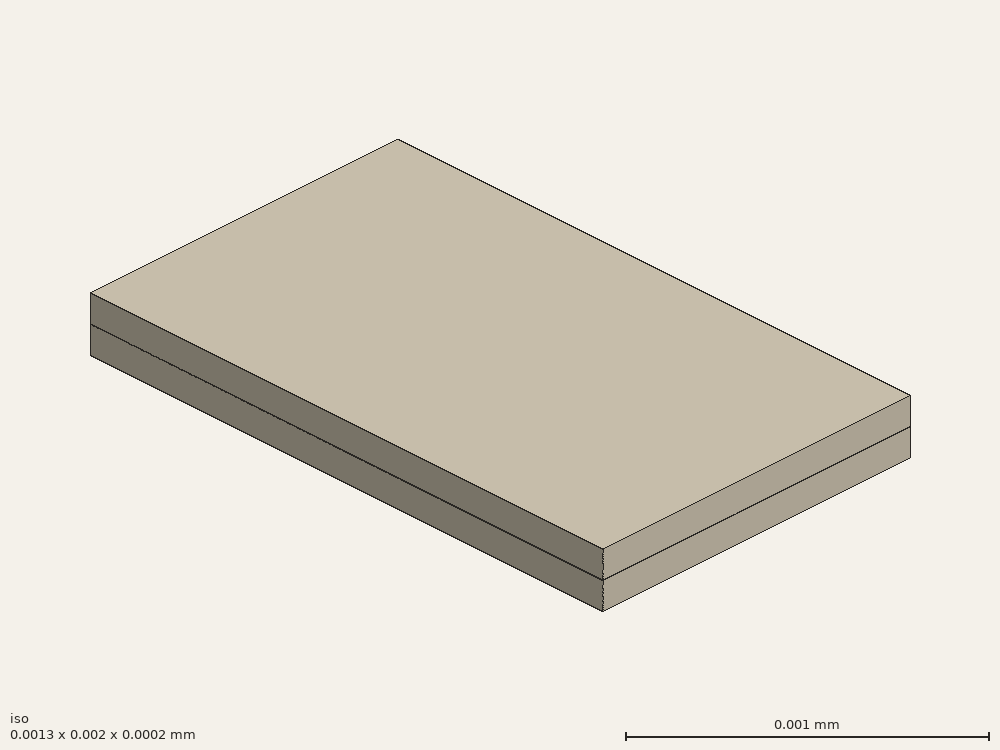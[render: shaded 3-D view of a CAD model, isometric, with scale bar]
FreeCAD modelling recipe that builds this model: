
FCSTD DOCUMENT  (FreeCAD 0.21R33694 (Git))
Label: diffPair
License: All rights reserved
LicenseURL: http://en.wikipedia.org/wiki/All_rights_reserved
objects: Part::Part2DObjectPython×23, App::FeaturePython×12, Part::Extrusion×5, Part::Cut×3, Part::FeaturePython×2
note: 33 computed .brp shape members not serialized (recipe doc carries the construction recipe); baked Part::Feature solids carry a one-line shape summary decoded from their .brp

FEATURE [Part::Part2DObjectPython] Wire  # Draft 2D object (typed FeaturePython)
  Area = 0.0014181
  ChamferSize = 0
  Closed = true
  End = (-0.05,0,0)
  FilletRadius = 0
  Length = 0.221006
  MakeFace = true
  Placement = pos=(-0.15,0,0) rot=(0,0,1;0rad)
  Points = (4) [(0,0,0),(0.00545955,0.015,0),(0.0945402,0.015,0),(0.1,-6.12323e-18,0)]
  Start = (-0.15,0,0)
  Subdivisions = 0
FEATURE [Part::Part2DObjectPython] Wire001  # Draft 2D object (typed FeaturePython)
  Area = 0.0014181
  ChamferSize = 0
  Closed = true
  End = (0.15,0,0)
  FilletRadius = 0
  Length = 0.221006
  MakeFace = true
  Placement = pos=(0.05,0,0) rot=(0,0,1;0rad)
  Points = (4) [(0,0,0),(0.00545955,0.015,0),(0.0945402,0.015,0),(0.1,-6.12323e-18,0)]
  Start = (0.05,0,0)
  Subdivisions = 0
FEATURE [Part::Part2DObjectPython] Rectangle  # Draft 2D object (typed FeaturePython)
  Area = 0.13
  ChamferSize = 0
  Columns = 1
  FilletRadius = 0
  Height = 0.1
  Length = 1.3
  MakeFace = true
  Placement = pos=(-0.65,-0.1,0) rot=(0,0,1;0rad)
  Rows = 1
FEATURE [Part::Part2DObjectPython] Rectangle001  # Draft 2D object (typed FeaturePython)
  Area = 0.13
  ChamferSize = 0
  Columns = 1
  FilletRadius = 0
  Height = 0.1
  Length = 1.3
  MakeFace = true
  Placement = pos=(-0.65,0,0) rot=(0,0,1;0rad)
  Rows = 1
FEATURE [Part::Part2DObjectPython] Clone2D  label="Wire (2D)"  # Draft 2D object (typed FeaturePython)
  Fuse = false
  Objects = -> [Wire]
  Placement = pos=(-0.15,0,0) rot=(0,0,1;0rad)
  Scale = (1,1,1)
FEATURE [Part::Part2DObjectPython] Clone2D001  label="Wire001 (2D)"  # Draft 2D object (typed FeaturePython)
  Fuse = false
  Objects = -> [Wire001]
  Placement = pos=(0.05,0,0) rot=(0,0,1;0rad)
  Scale = (1,1,1)
FEATURE [Part::Part2DObjectPython] Clone2D002  label="Rectangle (2D)"  # Draft 2D object (typed FeaturePython)
  Fuse = false
  Objects = -> [Rectangle]
  Placement = pos=(-0.65,-0.1,0) rot=(0,0,1;0rad)
  Scale = (1,1,1)
FEATURE [Part::Part2DObjectPython] Clone2D003  label="Rectangle001 (2D)"  # Draft 2D object (typed FeaturePython)
  Fuse = false
  Objects = -> [Rectangle001]
  Placement = pos=(-0.65,0,0) rot=(0,0,1;0rad)
  Scale = (1,1,1)
FEATURE [Part::Part2DObjectPython] Clone2D004  label="Wire (2D)001"  # Draft 2D object (typed FeaturePython)
  Fuse = false
  Objects = -> [Wire]
  Placement = pos=(-0.15,0,0) rot=(0,0,1;0rad)
  Scale = (1,1,1)
FEATURE [Part::Part2DObjectPython] Clone2D005  label="Wire001 (2D)001"  # Draft 2D object (typed FeaturePython)
  Fuse = false
  Objects = -> [Wire001]
  Placement = pos=(0.05,0,0) rot=(0,0,1;0rad)
  Scale = (1,1,1)
FEATURE [Part::Part2DObjectPython] Clone2D006  label="Rectangle (2D)001"  # Draft 2D object (typed FeaturePython)
  Fuse = false
  Objects = -> [Rectangle]
  Placement = pos=(-0.65,-0.1,0) rot=(0,0,1;0rad)
  Scale = (1,1,1)
FEATURE [Part::Part2DObjectPython] Clone2D007  label="Rectangle001 (2D)001"  # Draft 2D object (typed FeaturePython)
  Fuse = false
  Objects = -> [Rectangle001]
  Placement = pos=(-0.65,0,0) rot=(0,0,1;0rad)
  Scale = (1,1,1)
FEATURE [Part::Extrusion] Extrude004
  Base = -> Clone2D
  Dir = (0,0,1)
  DirMode = 2
  FaceMakerClass = Part::FaceMakerBullseye
  LengthFwd = 2
  LengthRev = 0
  Solid = false
  Symmetric = false
FEATURE [Part::Extrusion] Extrude005
  Base = -> Clone2D001
  Dir = (0,0,1)
  DirMode = 2
  FaceMakerClass = Part::FaceMakerBullseye
  LengthFwd = 2
  LengthRev = 0
  Solid = false
  Symmetric = false
FEATURE [Part::Extrusion] Extrude006
  Base = -> Clone2D002
  Dir = (0,0,1)
  DirMode = 2
  FaceMakerClass = Part::FaceMakerBullseye
  LengthFwd = 2
  LengthRev = 0
  Solid = false
  Symmetric = false
FEATURE [Part::Extrusion] Extrude007
  Base = -> Clone2D003
  Dir = (0,0,1)
  DirMode = 2
  FaceMakerClass = Part::FaceMakerBullseye
  LengthFwd = 2
  LengthRev = 0
  Solid = false
  Symmetric = false
FEATURE [Part::Cut] Cut002
  Base = -> Extrude007
  Tool = -> Extrude004
FEATURE [Part::Cut] Cut003
  Base = -> Cut002
  Tool = -> Extrude005
FEATURE [App::FeaturePython] Text010  label="_Sin(PV){port1}"  # WARN: FeaturePython — macro-defined, semantics opaque (R4)
  Placement = pos=(5.00075,-5.09743,10) rot=(0,0,1;0rad)
  Text = .
FEATURE [App::FeaturePython] Text011  label="_Sout(PV){port2}"  # WARN: FeaturePython — macro-defined, semantics opaque (R4)
  Placement = pos=(5.00075,-5.09743,10) rot=(0,0,1;0rad)
  Text = .
FEATURE [App::FeaturePython] Text012  label="_Lin(1,voltage,in1){v11}"  # WARN: FeaturePython — macro-defined, semantics opaque (R4)
  Placement = pos=(5.00075,-5.09743,10) rot=(0,0,1;0rad)
  Text = .
FEATURE [App::FeaturePython] Text013  label="_Lin(1,current,in1){i11}"  # WARN: FeaturePython — macro-defined, semantics opaque (R4)
  Placement = pos=(5.00075,-5.09743,10) rot=(0,0,1;0rad)
  Text = .
FEATURE [App::FeaturePython] Text014  label="_Lin(2,voltage,in2){v12}"  # WARN: FeaturePython — macro-defined, semantics opaque (R4)
  Placement = pos=(5.00075,-5.09743,10) rot=(0,0,1;0rad)
  Text = .
FEATURE [App::FeaturePython] Text015  label="_Lin(2,current,in2){i12}"  # WARN: FeaturePython — macro-defined, semantics opaque (R4)
  Placement = pos=(5.00075,-5.09743,10) rot=(0,0,1;0rad)
  Text = .
FEATURE [App::FeaturePython] Text016  label="_Lout(3,voltage,out3){v21}"  # WARN: FeaturePython — macro-defined, semantics opaque (R4)
  Placement = pos=(5.00075,-5.09743,10) rot=(0,0,1;0rad)
  Text = .
FEATURE [App::FeaturePython] Text017  label="_Lout(3,current,out3){i21}"  # WARN: FeaturePython — macro-defined, semantics opaque (R4)
  Placement = pos=(5.00075,-5.09743,10) rot=(0,0,1;0rad)
  Text = .
FEATURE [App::FeaturePython] Text018  label="_Lout(4,voltage,out4){v22}"  # WARN: FeaturePython — macro-defined, semantics opaque (R4)
  Placement = pos=(5.00075,-5.09743,10) rot=(0,0,1;0rad)
  Text = .
FEATURE [App::FeaturePython] Text019  label="_Lout(4,current,out4){i22}"  # WARN: FeaturePython — macro-defined, semantics opaque (R4)
  Placement = pos=(5.00075,-5.09743,10) rot=(0,0,1;0rad)
  Text = .
FEATURE [Part::Part2DObjectPython] Wire006  label="_Pi22"  # Draft 2D object (typed FeaturePython)
  Area = 1.4181e-09
  ChamferSize = 0
  Closed = true
  End = (5e-05,-0.0999,4.995)
  FilletRadius = 0
  Length = 0.000221006
  MakeFace = true
  Placement = pos=(0.00015,-0.0999,4.995) rot=(0.57735,0.57735,0.57735;4.18879rad)
  Points = (4) [(0,0,0),(1.5e-05,-5.45983e-06,0),(1.5e-05,-9.45404e-05,0),(0,-0.0001,0)]
  Start = (0.00015,-0.0999,4.995)
  Subdivisions = 0
FEATURE [Part::Part2DObjectPython] Wire007  label="_Pi21"  # Draft 2D object (typed FeaturePython)
  Area = 1.4181e-09
  ChamferSize = 0
  Closed = true
  End = (-0.00015,-0.0999,4.995)
  FilletRadius = 0
  Length = 0.000221006
  MakeFace = true
  Placement = pos=(-5e-05,-0.0999,4.995) rot=(0.57735,0.57735,0.57735;4.18879rad)
  Points = (4) [(0,0,0),(1.5e-05,-5.45983e-06,0),(1.5e-05,-9.45404e-05,0),(0,-0.0001,0)]
  Start = (-5e-05,-0.0999,4.995)
  Subdivisions = 0
FEATURE [Part::Part2DObjectPython] Wire008  label="_Pi11"  # Draft 2D object (typed FeaturePython)
  Area = 1.4181e-09
  ChamferSize = 0
  Closed = true
  End = (-5e-05,-0.1019,4.995)
  FilletRadius = 0
  Length = 0.000221006
  MakeFace = true
  Placement = pos=(-0.00015,-0.1019,4.995) rot=(1,0,0;1.5708rad)
  Points = (4) [(0,0,0),(5.45955e-06,1.5e-05,0),(9.45402e-05,1.5e-05,0),(0.0001,0,0)]
  Start = (-0.00015,-0.1019,4.995)
  Subdivisions = 0
FEATURE [Part::Part2DObjectPython] Wire009  label="_Pi12"  # Draft 2D object (typed FeaturePython)
  Area = 1.4181e-09
  ChamferSize = 0
  Closed = true
  End = (0.00015,-0.1019,4.995)
  FilletRadius = 0
  Length = 0.000221006
  MakeFace = true
  Placement = pos=(5e-05,-0.1019,4.995) rot=(1,0,0;1.5708rad)
  Points = (4) [(0,0,0),(5.45955e-06,1.5e-05,0),(9.45402e-05,1.5e-05,0),(0.0001,0,0)]
  Start = (5e-05,-0.1019,4.995)
  Subdivisions = 0
FEATURE [Part::Part2DObjectPython] Rectangle013  label="_Pport1"  # Draft 2D object (typed FeaturePython)
  Area = 2.6e-07
  ChamferSize = 0
  Columns = 1
  FilletRadius = 0
  Height = 0.0002
  Length = 0.0013
  MakeFace = true
  Placement = pos=(-0.00065,-0.1019,4.9949) rot=(1,0,0;1.5708rad)
  Rows = 1
FEATURE [Part::Part2DObjectPython] Line  label="_Pv11"  # Draft 2D object (typed FeaturePython)
  Area = 0
  ChamferSize = 0
  Closed = false
  End = (-0.0001,-0.1019,4.995)
  FilletRadius = 0
  Length = 0.0001
  MakeFace = true
  Placement = pos=(0,-0.1019,4.9949) rot=(1,0,0;1.5708rad)
  Points = (2) [(-0.0001,0,0),(-0.0001,0.0001,0)]
  Start = (-0.0001,-0.1019,4.9949)
  Subdivisions = 0
FEATURE [Part::Part2DObjectPython] Line004  label="_Pv12"  # Draft 2D object (typed FeaturePython)
  Area = 0
  ChamferSize = 0
  Closed = false
  End = (0.0001,-0.1019,4.995)
  FilletRadius = 0
  Length = 0.0001
  MakeFace = true
  Placement = pos=(0,-0.1019,4.9949) rot=(1,0,0;1.5708rad)
  Points = (2) [(0.0001,0,0),(0.0001,0.0001,0)]
  Start = (0.0001,-0.1019,4.9949)
  Subdivisions = 0
FEATURE [Part::Part2DObjectPython] Rectangle014  label="_Pport2"  # Draft 2D object (typed FeaturePython)
  Area = 2.6e-07
  ChamferSize = 0
  Columns = 1
  FilletRadius = 0
  Height = 0.0013
  Length = 0.0002
  MakeFace = true
  Placement = pos=(-0.00065,-0.0999,4.9949) rot=(0.57735,0.57735,0.57735;4.18879rad)
  Rows = 1
FEATURE [Part::Part2DObjectPython] Line005  label="_Pv21"  # Draft 2D object (typed FeaturePython)
  Area = 0
  ChamferSize = 0
  Closed = false
  End = (-0.0001,-0.0999,4.995)
  FilletRadius = 0
  Length = 0.0001
  MakeFace = true
  Placement = pos=(0,-0.0999,4.9949) rot=(0.57735,0.57735,0.57735;4.18879rad)
  Points = (2) [(1.38778e-17,-0.0001,0),(0.0001,-0.0001,0)]
  Start = (-0.0001,-0.0999,4.9949)
  Subdivisions = 0
FEATURE [Part::Part2DObjectPython] Line006  label="_Pv22"  # Draft 2D object (typed FeaturePython)
  Area = 0
  ChamferSize = 0
  Closed = false
  End = (0.0001,-0.0999,4.995)
  FilletRadius = 0
  Length = 0.0001
  MakeFace = true
  Placement = pos=(0,-0.0999,4.9949) rot=(0.57735,0.57735,0.57735;4.18879rad)
  Points = (2) [(1.38778e-17,0.0001,0),(0.0001,0.0001,0)]
  Start = (0.0001,-0.0999,4.9949)
  Subdivisions = 0
FEATURE [Part::Part2DObjectPython] Rectangle015  # Draft 2D object (typed FeaturePython)
  Area = 0.01
  ChamferSize = 0
  Columns = 1
  FilletRadius = 0
  Height = 0.1
  Length = 0.1
  MakeFace = true
  Placement = pos=(-0.15,0,2.45) rot=(1,0,0;1.5708rad)
  Rows = 1
FEATURE [Part::Extrusion] Extrude
  Base = -> Rectangle015
  Dir = (0,-1,2e-16)
  DirMode = 2
  FaceMakerClass = Part::FaceMakerBullseye
  LengthFwd = 0.1
  LengthRev = 0
  Placement = pos=(0,0,-1.5) rot=(0,0,1;0rad)
  Solid = false
  Symmetric = false
FEATURE [Part::Cut] Cut
  Base = -> Extrude006
  Tool = -> Extrude
FEATURE [Part::FeaturePython] BooleanFragments  # WARN: FeaturePython — macro-defined, semantics opaque (R4)
  Mode = 0
  Objects = -> [Cut003,Cut]
  Tolerance = 0
FEATURE [Part::FeaturePython] Clone  label="scaled"  # Draft clone (typed FeaturePython)
  AttacherType = Attacher::AttachEngine3D
  Fuse = false
  Objects = -> [BooleanFragments]
  Placement = pos=(0,-0.0999,4.995) rot=(1,0,0;1.5708rad)
  Scale = (0.001,0.001,0.001)
FEATURE [App::FeaturePython] Text020  label="_D(1,2)"  # WARN: FeaturePython — macro-defined, semantics opaque (R4)
  Placement = pos=(5.00075,-5.09743,10) rot=(0,0,1;0rad)
  Text = .
FEATURE [App::FeaturePython] Text021  label="_D(3,4)"  # WARN: FeaturePython — macro-defined, semantics opaque (R4)
  Placement = pos=(5.00075,-5.09743,10) rot=(0,0,1;0rad)
  Text = .
